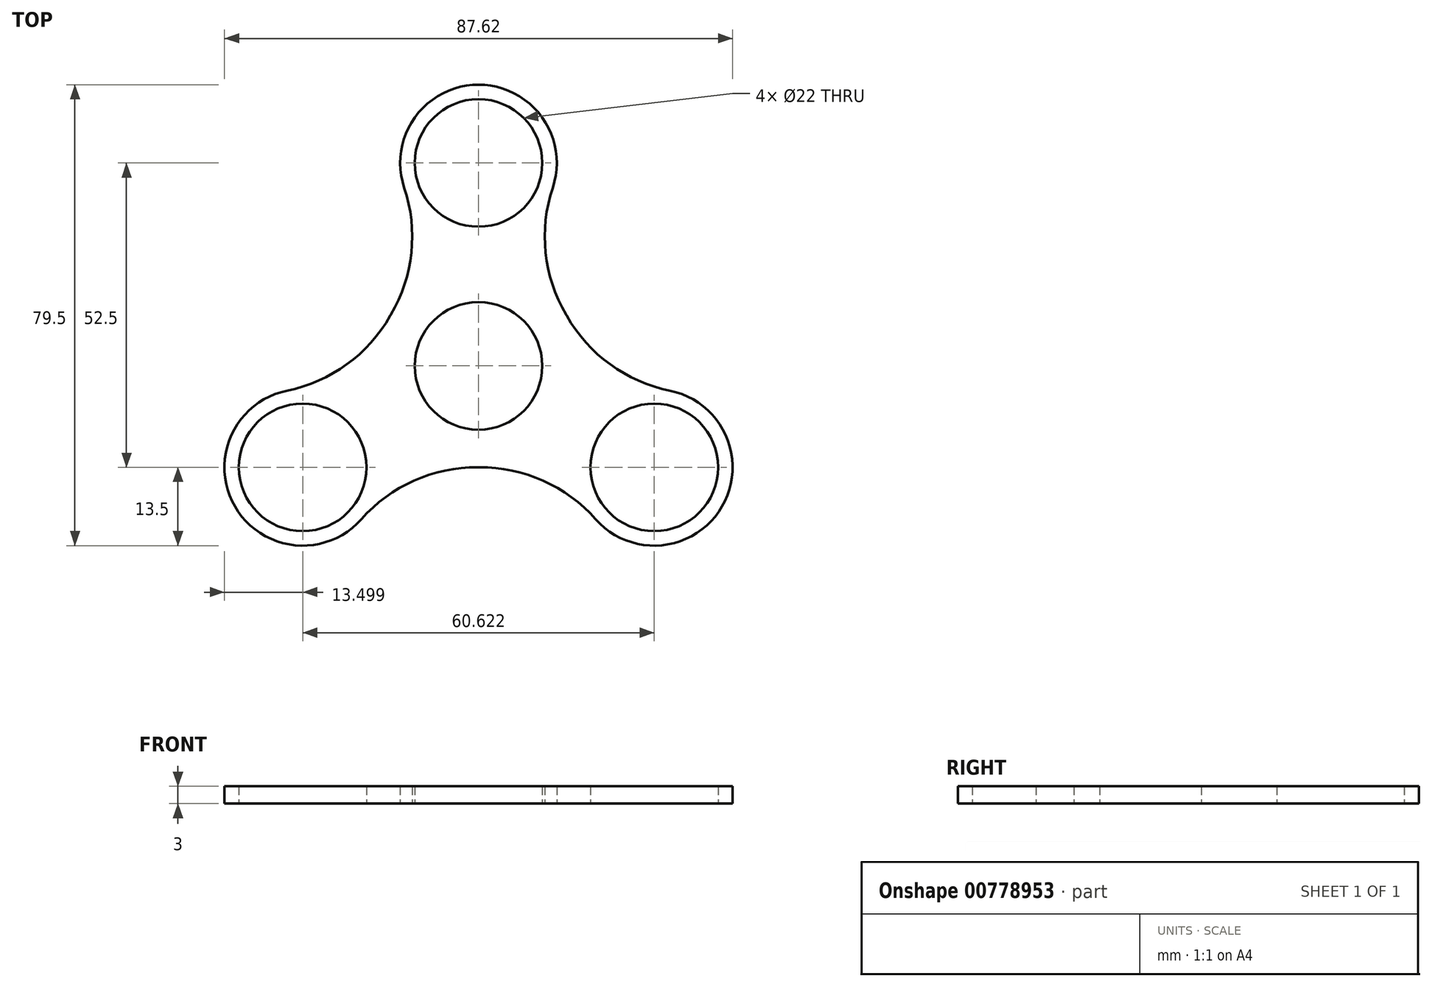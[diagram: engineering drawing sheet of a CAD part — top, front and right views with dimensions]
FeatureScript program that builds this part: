
annotation { "Feature Type Name" : "Feature", "Feature Type Description" : "" }
export const myFeature = defineFeature(function(context is Context, id is Id, definition is map)
    precondition{}
    {
        {
            var Q0;
            Q0=qCreatedBy(makeId("Top.planeOp"),FACE);
            var sketch = newSketch(context, id + "F0", { "sketchPlane" : qUnion([Q0])});
            skArc(sketch, "E0", {"start": v(9.53, 5.5) * mm, "mid": v(0, 11) * mm, "end": v(-9.53, 5.5) * mm});
            skCircle(sketch, "E1", {"center": v(0, 35) * mm, "radius": 11 * mm});
            skArc(sketch, "E2", {"start": v(15.16, 8.75) * mm, "mid": v(15.12, 8.8) * mm, "end": v(15.09, 8.87) * mm});
            skArc(sketch, "E3", {"start": v(12.8, 30.71) * mm, "mid": v(0, 48.5) * mm, "end": v(-12.8, 30.71) * mm});
            skPoint(sketch, "E4.bottom.start.orphan", {"position": v(11, 0) * mm});
            skArc(sketch, "E5", {"start": v(12.8, 30.71) * mm, "mid": v(11.57, 19.54) * mm, "end": v(15.09, 8.87) * mm});
            skArc(sketch, "E6.MirrorCS", {"start": v(-12.8, 30.71) * mm, "mid": v(-11.57, 19.54) * mm, "end": v(-15.09, 8.87) * mm});
            skCircle(sketch, "E7.1.0", {"center": v(-30.31, -17.5) * mm, "radius": 11 * mm});
            skArc(sketch, "E7.1.1", {"start": v(-33, -4.27) * mm, "mid": v(-42, -24.25) * mm, "end": v(-20.2, -26.44) * mm});
            skArc(sketch, "E7.1.2", {"start": v(-33, -4.27) * mm, "mid": v(-22.71, 0.25) * mm, "end": v(-15.22, 8.63) * mm});
            skArc(sketch, "E7.1.3", {"start": v(-20.2, -26.44) * mm, "mid": v(-11.14, -19.8) * mm, "end": v(-0.14, -17.5) * mm});
            skArc(sketch, "E7.1.4", {"start": v(-9.53, 5.5) * mm, "mid": v(-9.53, -5.5) * mm, "end": v(0, -11) * mm});
            skArc(sketch, "E7.1.5", {"start": v(-15.16, 8.75) * mm, "mid": v(-15.19, 8.7) * mm, "end": v(-15.22, 8.63) * mm});
            skCircle(sketch, "E7.2.0", {"center": v(30.31, -17.5) * mm, "radius": 11 * mm});
            skArc(sketch, "E7.2.1", {"start": v(20.2, -26.44) * mm, "mid": v(42, -24.25) * mm, "end": v(33, -4.27) * mm});
            skArc(sketch, "E7.2.2", {"start": v(20.2, -26.44) * mm, "mid": v(11.14, -19.8) * mm, "end": v(0.14, -17.5) * mm});
            skArc(sketch, "E7.2.3", {"start": v(33, -4.27) * mm, "mid": v(22.71, 0.25) * mm, "end": v(15.22, 8.63) * mm});
            skArc(sketch, "E7.2.4", {"start": v(0, -11) * mm, "mid": v(9.53, -5.5) * mm, "end": v(9.53, 5.5) * mm});
            skArc(sketch, "E7.2.5", {"start": v(0, -17.5) * mm, "mid": v(0.07, -17.5) * mm, "end": v(0.14, -17.5) * mm});
            skArc(sketch, "E8.trimOffspring", {"start": v(-15.09, 8.87) * mm, "mid": v(-15.12, 8.8) * mm, "end": v(-15.16, 8.75) * mm});
            skArc(sketch, "E9.trimOffspring", {"start": v(-0.14, -17.5) * mm, "mid": v(-0.07, -17.5) * mm, "end": v(0, -17.5) * mm});
            skArc(sketch, "E10.trimOffspring", {"start": v(15.22, 8.63) * mm, "mid": v(15.19, 8.7) * mm, "end": v(15.16, 8.75) * mm});
            skSolve(sketch);
        }
        {
            var Q0;
            Q0=makeQuery(id+"F0.imprint","IMPRINT",FACE,{"disambiguationData":[TD([[makeQuery(id+"F0.imprint","IMPRINT",EDGE,{"derivedFrom":sQuery(id+"F0.wireOp",EDGE,"E0")}),-1.0]])]});
            extrude(context, id + "F1", {"entities" : qUnion([Q0]), "depth" : 3 * mm, "offsetDistance" : 25 * mm});
        }
    });
